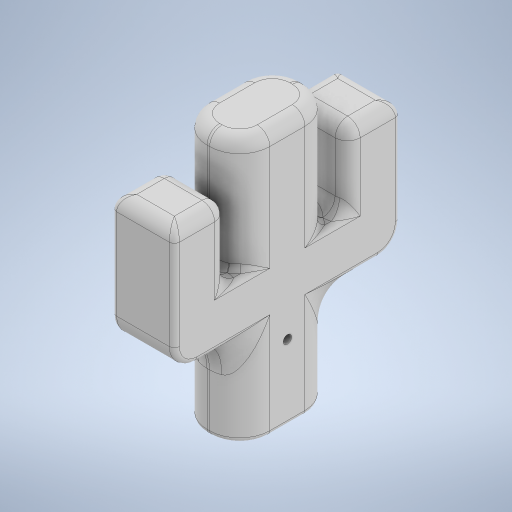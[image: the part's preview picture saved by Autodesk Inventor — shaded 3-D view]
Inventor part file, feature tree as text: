
AUTODESK INVENTOR PART (.ipt)
format: ipt  version: 2023 (Build 270158000, 158)  size: 715,776 bytes
history: native  units: mm
features: fillet x8, sketch x7, extrude x7, plane x2
ambient origin geometry x8: Origin, YZ Plane, XZ Plane, XY Plane, X Axis, Y Axis, Z Axis, Center Point
bodies: Solid1 (feature_tree)
feature tree (24):
  sketch  "Sketch1"  dims[d0=254.0mm d1=170.0mm]
  plane  "Work Plane1"
  extrude  "Extrusion1"  Depth=170.0mm
  extrude  "Extrusion2"  Depth=38.0mm
  fillet  "Fillet1"  Radius=25.0mm
  plane  "Work Plane2"
  extrude  "Extrusion3"  Depth=12.0mm
  extrude  "Extrusion4"  Depth=12.0mm
  extrude  "Extrusion5"  Depth=38.0mm
  fillet  "Fillet2"  Radius=25.0mm
  extrude  "Extrusion6"  Depth=5.0mm TaperAngle=0.0deg
  fillet  "Fillet3"  Radius=5.0mm
  fillet  "Fillet4"  [1 undecoded]
  fillet  "Fillet5"  Radius=90.0mm
  fillet  "Fillet9"  Radius=25.0mm
  fillet  "Fillet10"  Radius=20.0mm
  extrude  "Extrusion7"  Depth=2.0mm TaperAngle=0.0deg
  fillet  "Fillet11"  Radius=5.0mm
  sketch  "Sketch2"  dims[d2=17.0mm d4=38.0mm d5=25.0mm]
  sketch  "Sketch3"  dims[d6=12.0mm d7=12.0mm]
  sketch  "Sketch4"  dims[d8=12.0mm d9=12.0mm]
  sketch  "Sketch5"  dims[d10=100.0mm d11=0.0mm d12=38.0mm d13=25.0mm]
  sketch  "Sketch7"  dims[d14=12.0mm d15=5.0mm d16=0.0mm d17=5.0mm d18=-60.0mm d19=90.0mm d20=25.0mm d21=20.0mm d22=0.0mm]
  sketch  "Sketch8"  dims[d23=17.0mm d24=50.0mm d25=0.0mm d26=5.0mm d27=5.0mm d28=30.0mm d29=0.0mm d30=2.0mm d31=3.3mm d32=70.0mm d33=0.0mm d34=0.0mm d35=5.0mm d36=5.0mm d37=2.0mm d39=10.0mm d40=10.0mm d41=10.0mm d42=0.0mm d45=5.0mm d46=17.0mm d47=0.0mm d48=0.0mm d49=2.0mm d43=0.0mm d44=0.0mm]
note: 1 required parameter value undecoded (feature->parameter linkage not recoverable at this tier; creation-order binding heuristic only, values carry confidence <= 0.55)
